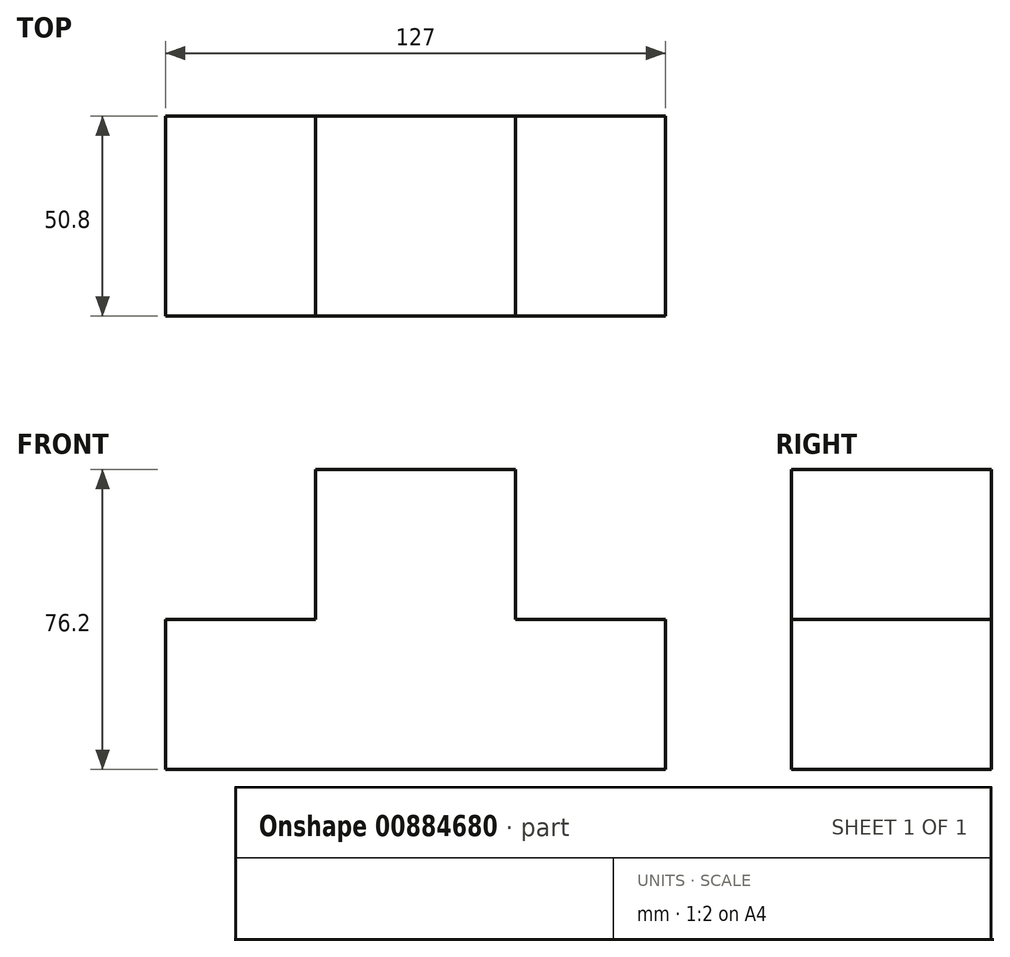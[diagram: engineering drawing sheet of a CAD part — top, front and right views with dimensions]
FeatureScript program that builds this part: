
annotation { "Feature Type Name" : "Feature", "Feature Type Description" : "" }
export const myFeature = defineFeature(function(context is Context, id is Id, definition is map)
    precondition{}
    {
        {
            var Q0;
            Q0=qCreatedBy(makeId("Front.planeOp"),FACE);
            var sketch = newSketch(context, id + "F0", { "sketchPlane" : qUnion([Q0])});
            skLineSegment(sketch, "E0", {"start": v(-47.17, 5.73) * mm, "end": v(79.83, 5.73) * mm});
            skLineSegment(sketch, "E1", {"start": v(79.83, 5.73) * mm, "end": v(79.83, -32.37) * mm});
            skLineSegment(sketch, "E2", {"start": v(79.83, -32.37) * mm, "end": v(-47.17, -32.37) * mm});
            skLineSegment(sketch, "E3", {"start": v(-47.17, -32.37) * mm, "end": v(-47.17, 5.73) * mm});
            skLineSegment(sketch, "E4", {"start": v(-9.07, 5.73) * mm, "end": v(-9.07, 43.83) * mm});
            skLineSegment(sketch, "E5", {"start": v(-9.07, 43.83) * mm, "end": v(41.73, 43.83) * mm});
            skLineSegment(sketch, "E6", {"start": v(41.73, 43.83) * mm, "end": v(41.73, 5.73) * mm});
            skSolve(sketch);
        }
        {
            var Q0;
            Q0 = qSketchRegion(id + "F0", true);
            extrude(context, id + "F1", {"entities" : qUnion([Q0]), "depth" : 50.8 * mm, "offsetDistance" : 25.4 * mm});
        }
    });
